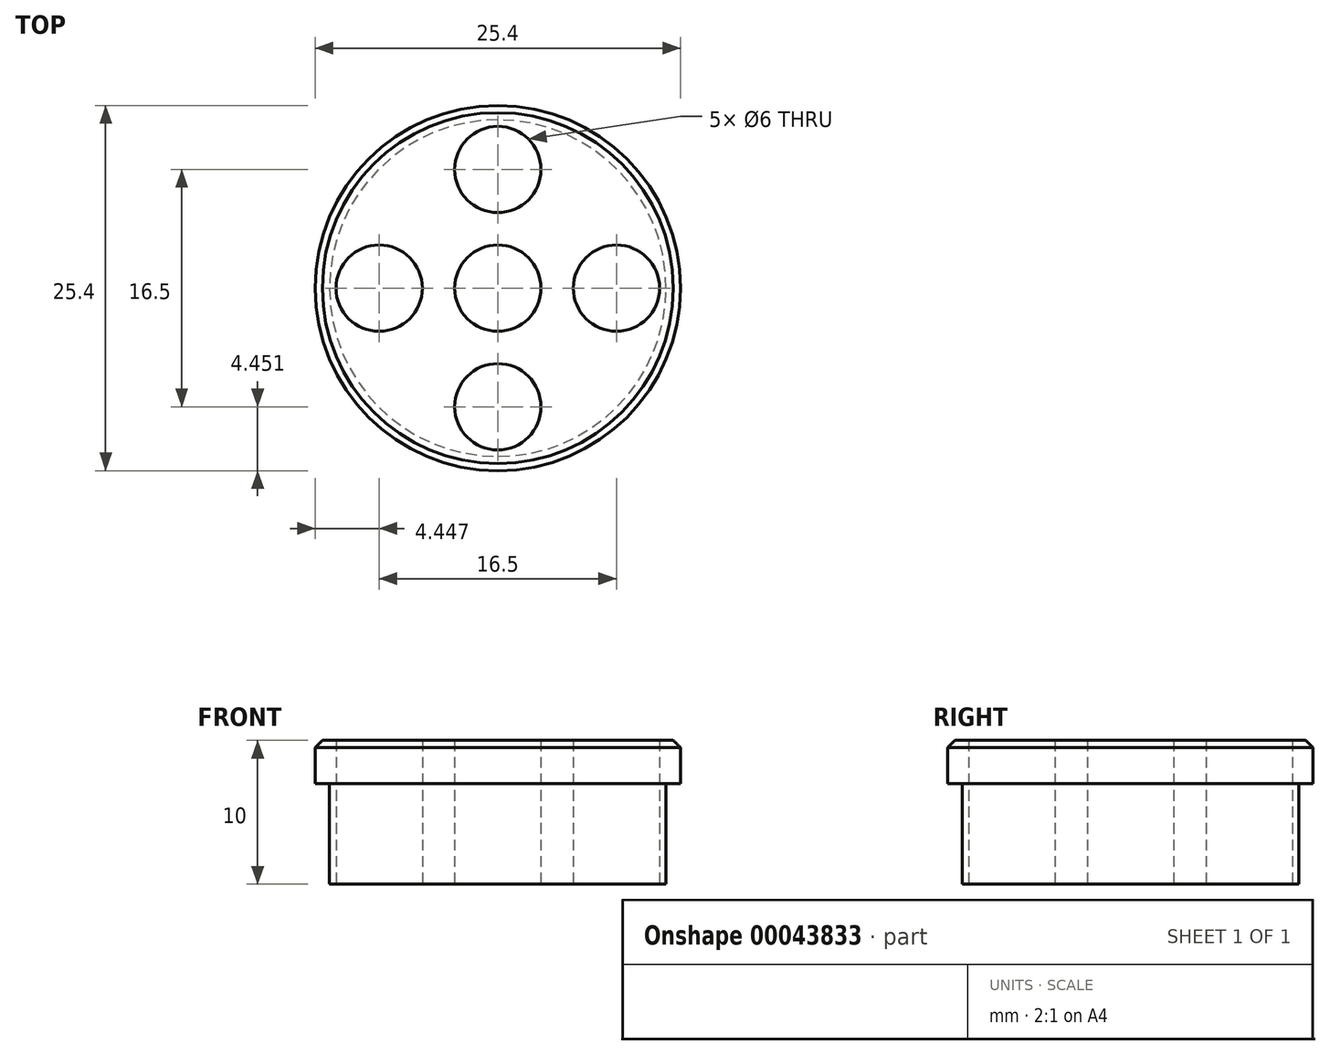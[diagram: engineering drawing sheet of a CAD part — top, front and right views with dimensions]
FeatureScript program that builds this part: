
annotation { "Feature Type Name" : "Feature", "Feature Type Description" : "" }
export const myFeature = defineFeature(function(context is Context, id is Id, definition is map)
    precondition{}
    {
        {
            var Q0;
            Q0=qCreatedBy(makeId("Top.planeOp"),FACE);
            var sketch = newSketch(context, id + "F0", { "sketchPlane" : qUnion([Q0])});
            skCircle(sketch, "E0", {"center": v(0.26, -0.07) * mm, "radius": 3 * mm});
            skLineSegment(sketch, "E1", {"start": v(0.26, -0.07) * mm, "end": v(-31.5, -0.07) * mm, "construction": true});
            skLineSegment(sketch, "E2", {"start": v(0.26, -0.07) * mm, "end": v(0.26, 24.28) * mm, "construction": true});
            skLineSegment(sketch, "E3", {"start": v(0.26, -0.07) * mm, "end": v(26.35, -0.07) * mm, "construction": true});
            skLineSegment(sketch, "E4", {"start": v(0.26, -0.07) * mm, "end": v(0.26, -22.9) * mm, "construction": true});
            skCircle(sketch, "E5", {"center": v(8.5, -0.07) * mm, "radius": 3 * mm});
            skCircle(sketch, "E6.MirrorC", {"center": v(-8, -0.07) * mm, "radius": 3 * mm});
            skCircle(sketch, "E7", {"center": v(0.26, -0.07) * mm, "radius": 12.7 * mm});
            skCircle(sketch, "E8", {"center": v(0.26, -0.07) * mm, "radius": 8.25 * mm, "construction": true});
            skCircle(sketch, "E9", {"center": v(0.26, 8.18) * mm, "radius": 3 * mm});
            skCircle(sketch, "E10.MirrorC", {"center": v(0.26, -8.32) * mm, "radius": 3 * mm});
            skSolve(sketch);
        }
        {
            var Q0;
            Q0=makeQuery(id+"F0.imprint","IMPRINT",FACE,{"disambiguationData":[TD([[makeQuery(id+"F0.imprint","IMPRINT",EDGE,{"derivedFrom":sQuery(id+"F0.wireOp",EDGE,"E0")}),-1.0]])]});
            extrude(context, id + "F1", {"entities" : qUnion([Q0]), "depth" : 10 * mm});
        }
        {
            var Q0;
            Q0=makeQuery(id+"F1.opExtrude","CAP_FACE",FACE,{"disambiguationData":[OSD([sQuery(id+"F0.wireOp",EDGE,"E0"),sQuery(id+"F0.wireOp",EDGE,"E5"),sQuery(id+"F0.wireOp",EDGE,"E6.MirrorC"),sQuery(id+"F0.wireOp",EDGE,"E7"),sQuery(id+"F0.wireOp",EDGE,"E9"),sQuery(id+"F0.wireOp",EDGE,"E10.MirrorC")])],"isStart":true});
            var sketch = newSketch(context, id + "F2", { "sketchPlane" : qUnion([Q0])});
            skCircle(sketch, "E11.0", {"center": v(0.26, 0.07) * mm, "radius": 12.7 * mm});
            skCircle(sketch, "E12.0", {"center": v(0.26, 0.07) * mm, "radius": 11.7 * mm});
            skSolve(sketch);
        }
        {
            var Q0;
            Q0=makeQuery(id+"F2.imprint","IMPRINT",FACE,{"disambiguationData":[TD([[makeQuery(id+"F2.imprint","IMPRINT",EDGE,{"derivedFrom":sQuery(id+"F2.wireOp",EDGE,"E11.0")}),-1.0]])]});
            extrude(context, id + "F3", {"entities" : qUnion([Q0]), "operationType" : NewBodyOperationType.REMOVE, "oppositeDirection" : true, "depth" : 7 * mm});
        }
        {
            var Q0;
            Q0=makeQuery(id+"F1.opExtrude","CAP_EDGE",EDGE,{"disambiguationData":[OSD([sQuery(id+"F0.wireOp",EDGE,"E7")])],"isStart":false});
            var Q1;
            Q1=makeQuery(id+"F3.boolean.opBoolean","COPY",EDGE,{"derivedFrom":makeQuery(id+"F3.opExtrude","CAP_EDGE",EDGE,{"disambiguationData":[OSD([sQuery(id+"F2.wireOp",EDGE,"E12.0")])],"isStart":true})});
            chamfer(context, id + "F4", {"entities" : qUnion([Q0, Q1]), "width" : 0.5 * mm, "tangentPropagation" : true});
        }
    });
